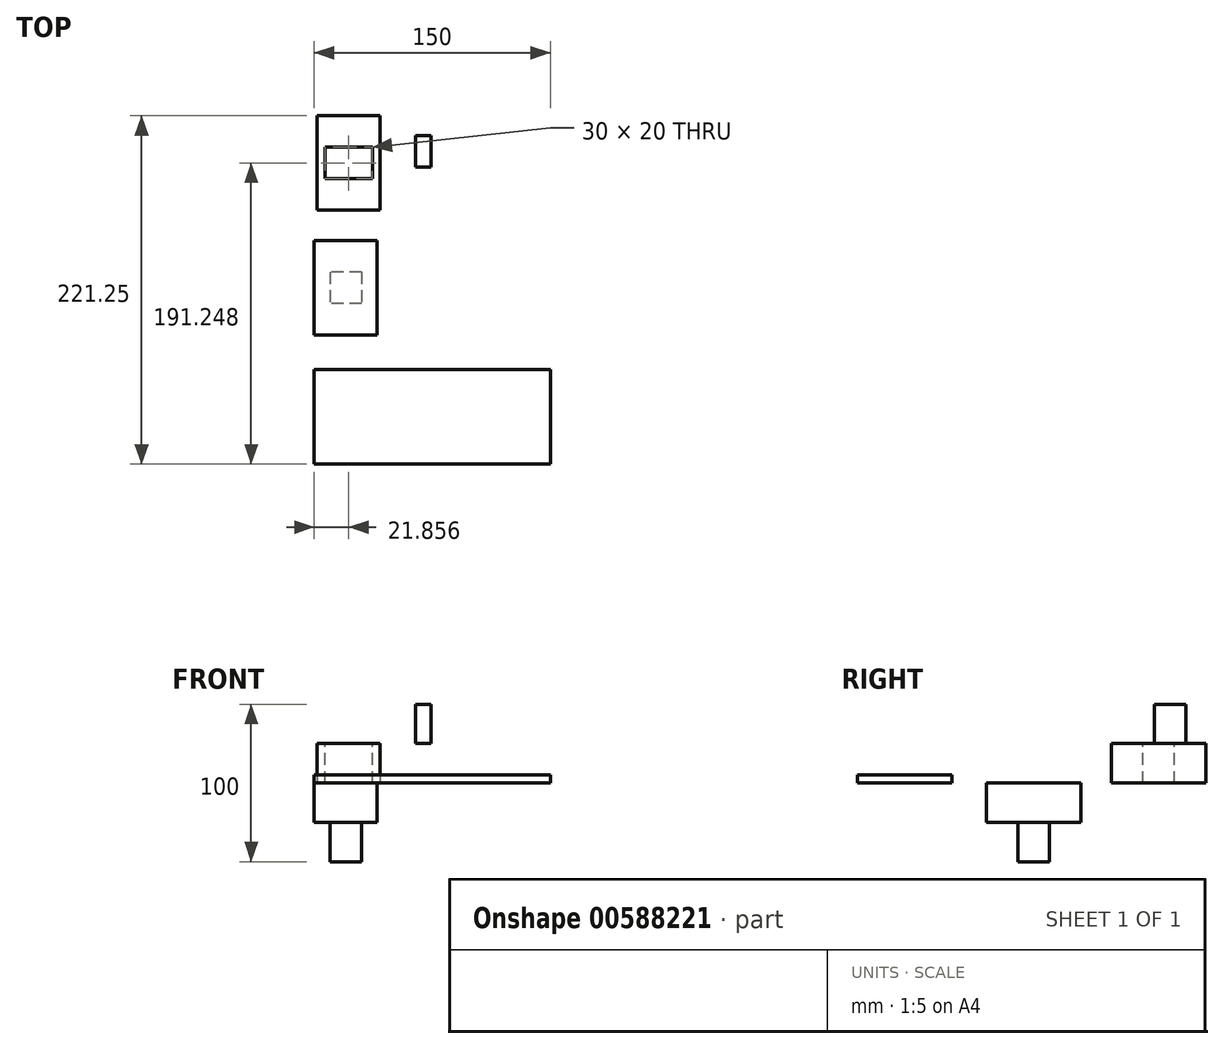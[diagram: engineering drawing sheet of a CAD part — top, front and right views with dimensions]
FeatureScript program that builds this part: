
annotation { "Feature Type Name" : "Feature", "Feature Type Description" : "" }
export const myFeature = defineFeature(function(context is Context, id is Id, definition is map)
    precondition{}
    {
        {
            var Q0;
            Q0=qCreatedBy(makeId("Top.planeOp"),FACE);
            var sketch = newSketch(context, id + "F0", { "sketchPlane" : qUnion([Q0])});
            skLineSegment(sketch, "E0.bottom", {"start": v(-49.84, 79.3) * mm, "end": v(-9.84, 79.3) * mm});
            skLineSegment(sketch, "E0.top", {"start": v(-49.84, 19.3) * mm, "end": v(-9.84, 19.3) * mm});
            skLineSegment(sketch, "E0.left", {"start": v(-49.84, 79.3) * mm, "end": v(-49.84, 19.3) * mm});
            skLineSegment(sketch, "E0.right", {"start": v(-9.84, 79.3) * mm, "end": v(-9.84, 19.3) * mm});
            skLineSegment(sketch, "E1.bottom", {"start": v(-51.7, 0) * mm, "end": v(-11.7, 0) * mm});
            skLineSegment(sketch, "E1.top", {"start": v(-51.7, -60) * mm, "end": v(-11.7, -60) * mm});
            skLineSegment(sketch, "E1.left", {"start": v(-51.7, 0) * mm, "end": v(-51.7, -60) * mm});
            skLineSegment(sketch, "E1.right", {"start": v(-11.7, 0) * mm, "end": v(-11.7, -60) * mm});
            skPoint(sketch, "E2.centerSnap0", {"position": v(-51.7, -30) * mm});
            skPoint(sketch, "E2.centerSnap1", {"position": v(-31.7, 0) * mm});
            skLineSegment(sketch, "E3.bottom", {"start": v(-51.7, -81.95) * mm, "end": v(98.3, -81.95) * mm});
            skLineSegment(sketch, "E3.top", {"start": v(-51.7, -141.95) * mm, "end": v(98.3, -141.95) * mm});
            skLineSegment(sketch, "E3.left", {"start": v(-51.7, -81.95) * mm, "end": v(-51.7, -141.95) * mm});
            skLineSegment(sketch, "E3.right", {"start": v(98.3, -81.95) * mm, "end": v(98.3, -141.95) * mm});
            skSolve(sketch);
        }
        {
            var Q0;
            Q0=makeQuery(id+"F0.imprint","IMPRINT",FACE,{"disambiguationData":[TD([[makeQuery(id+"F0.imprint","IMPRINT",EDGE,{"derivedFrom":sQuery(id+"F0.wireOp",EDGE,"E0.bottom")}),-1.0]])]});
            extrude(context, id + "F1", {"entities" : qUnion([Q0]), "depth" : 25 * mm, "offsetDistance" : 25 * mm});
        }
        {
            var Q0;
            Q0=makeQuery(id+"F1.opExtrude","CAP_FACE",FACE,{"disambiguationData":[OSD([sQuery(id+"F0.wireOp",EDGE,"E0.bottom"),sQuery(id+"F0.wireOp",EDGE,"E0.top"),sQuery(id+"F0.wireOp",EDGE,"E0.left"),sQuery(id+"F0.wireOp",EDGE,"E0.right")])],"isStart":false});
            var sketch = newSketch(context, id + "F2", { "sketchPlane" : qUnion([Q0])});
            skLineSegment(sketch, "E4.bottom", {"start": v(-44.84, 59.3) * mm, "end": v(-14.84, 59.3) * mm});
            skLineSegment(sketch, "E4.top", {"start": v(-44.84, 39.3) * mm, "end": v(-14.84, 39.3) * mm});
            skLineSegment(sketch, "E4.left", {"start": v(-44.84, 59.3) * mm, "end": v(-44.84, 39.3) * mm});
            skLineSegment(sketch, "E4.right", {"start": v(-14.84, 59.3) * mm, "end": v(-14.84, 39.3) * mm});
            skPoint(sketch, "E4.middle", {"position": v(-29.84, 49.3) * mm});
            skPoint(sketch, "E4.middle.positionSnap0", {"position": v(-49.84, 49.3) * mm});
            skPoint(sketch, "E4.middle.positionSnap1", {"position": v(-29.84, 79.3) * mm});
            skPoint(sketch, "E4.centerSnap0", {"position": v(-49.84, 49.3) * mm});
            skPoint(sketch, "E4.centerSnap1", {"position": v(-29.84, 79.3) * mm});
            skLineSegment(sketch, "E5.bottom", {"start": v(22.62, 46.65) * mm, "end": v(12.62, 46.65) * mm});
            skLineSegment(sketch, "E5.top", {"start": v(22.62, 66.65) * mm, "end": v(12.62, 66.65) * mm});
            skLineSegment(sketch, "E5.left", {"start": v(22.62, 46.65) * mm, "end": v(22.62, 66.65) * mm});
            skLineSegment(sketch, "E5.right", {"start": v(12.62, 46.65) * mm, "end": v(12.62, 66.65) * mm});
            skPoint(sketch, "E5.middle", {"position": v(17.62, 56.65) * mm});
            skSolve(sketch);
        }
        {
            var Q0;
            Q0=makeQuery(id+"F2.imprint","IMPRINT",FACE,{"disambiguationData":[TD([[makeQuery(id+"F2.imprint","IMPRINT",EDGE,{"derivedFrom":sQuery(id+"F2.wireOp",EDGE,"E4.bottom")}),-1.0]])]});
            extrude(context, id + "F3", {"entities" : qUnion([Q0]), "operationType" : NewBodyOperationType.REMOVE, "oppositeDirection" : true, "depth" : 25 * mm, "offsetDistance" : 25 * mm});
        }
        {
            var Q0;
            Q0=makeQuery(id+"F0.imprint","IMPRINT",FACE,{"disambiguationData":[TD([[makeQuery(id+"F0.imprint","IMPRINT",EDGE,{"derivedFrom":sQuery(id+"F0.wireOp",EDGE,"E1.bottom")}),-1.0]])]});
            var Q1;
            Q1=makeQuery(id+"F0.imprint","IMPRINT",FACE,{"disambiguationData":[TD([[makeQuery(id+"F0.imprint","IMPRINT",EDGE,{"derivedFrom":sQuery(id+"F0.wireOp",EDGE,"E2")}),1.0]])]});
            extrude(context, id + "F4", {"entities" : qUnion([Q0, Q1]), "oppositeDirection" : true, "depth" : 25 * mm, "offsetDistance" : 25 * mm});
        }
        {
            var Q0;
            Q0=makeQuery(id+"F0.imprint","IMPRINT",FACE,{"disambiguationData":[TD([[makeQuery(id+"F0.imprint","IMPRINT",EDGE,{"derivedFrom":sQuery(id+"F0.wireOp",EDGE,"E3.bottom")}),-1.0]])]});
            extrude(context, id + "F5", {"entities" : qUnion([Q0]), "depth" : 5 * mm, "offsetDistance" : 25 * mm});
        }
        {
            var Q0;
            Q0=makeQuery(id+"F5.opExtrude","CAP_FACE",FACE,{"disambiguationData":[OSD([sQuery(id+"F0.wireOp",EDGE,"E3.bottom"),sQuery(id+"F0.wireOp",EDGE,"E3.top"),sQuery(id+"F0.wireOp",EDGE,"E3.left"),sQuery(id+"F0.wireOp",EDGE,"E3.right")])],"isStart":false});
            var sketch = newSketch(context, id + "F6", { "sketchPlane" : qUnion([Q0])});
            skLineSegment(sketch, "E6", {"start": v(-11.7, -81.95) * mm, "end": v(-11.7, -141.95) * mm});
            skLineSegment(sketch, "E7", {"start": v(58.3, -81.95) * mm, "end": v(58.3, -141.95) * mm});
            skSolve(sketch);
        }
        {
            var Q0;
            Q0=makeQuery(id+"F4.opExtrude","CAP_FACE",FACE,{"disambiguationData":[OSD([sQuery(id+"F0.wireOp",EDGE,"E1.bottom"),sQuery(id+"F0.wireOp",EDGE,"E1.top"),sQuery(id+"F0.wireOp",EDGE,"E1.left"),sQuery(id+"F0.wireOp",EDGE,"E1.right")])],"isStart":false});
            var sketch = newSketch(context, id + "F7", { "sketchPlane" : qUnion([Q0])});
            skPoint(sketch, "E8.middle", {"position": v(-32.72, -27.6) * mm});
            skLineSegment(sketch, "E9.bottom", {"start": v(-21.7, 20) * mm, "end": v(-41.7, 20) * mm});
            skLineSegment(sketch, "E9.top", {"start": v(-21.7, 40) * mm, "end": v(-41.7, 40) * mm});
            skLineSegment(sketch, "E9.left", {"start": v(-21.7, 20) * mm, "end": v(-21.7, 40) * mm});
            skLineSegment(sketch, "E9.right", {"start": v(-41.7, 20) * mm, "end": v(-41.7, 40) * mm});
            skPoint(sketch, "E9.middle", {"position": v(-31.7, 30) * mm});
            skPoint(sketch, "E9.middle.positionSnap0", {"position": v(-31.7, 0) * mm});
            skPoint(sketch, "E9.middle.positionSnap1", {"position": v(-51.7, 30) * mm});
            skPoint(sketch, "E9.centerSnap0", {"position": v(-31.7, 0) * mm});
            skPoint(sketch, "E9.centerSnap1", {"position": v(-51.7, 30) * mm});
            skSolve(sketch);
        }
        {
            var Q0;
            Q0=makeQuery(id+"F7.imprint","IMPRINT",FACE,{"disambiguationData":[TD([[makeQuery(id+"F7.imprint","IMPRINT",EDGE,{"derivedFrom":sQuery(id+"F7.wireOp",EDGE,"E9.bottom")}),-1.0]])]});
            extrude(context, id + "F8", {"entities" : qUnion([Q0]), "operationType" : NewBodyOperationType.ADD, "depth" : 25 * mm, "offsetDistance" : 25 * mm});
        }
        {
            var Q0;
            Q0=makeQuery(id+"F2.imprint","IMPRINT",FACE,{"disambiguationData":[TD([[makeQuery(id+"F2.imprint","IMPRINT",EDGE,{"derivedFrom":sQuery(id+"F2.wireOp",EDGE,"E5.bottom")}),-1.0]])]});
            extrude(context, id + "F9", {"entities" : qUnion([Q0]), "depth" : 25 * mm, "offsetDistance" : 25 * mm});
        }
    });
